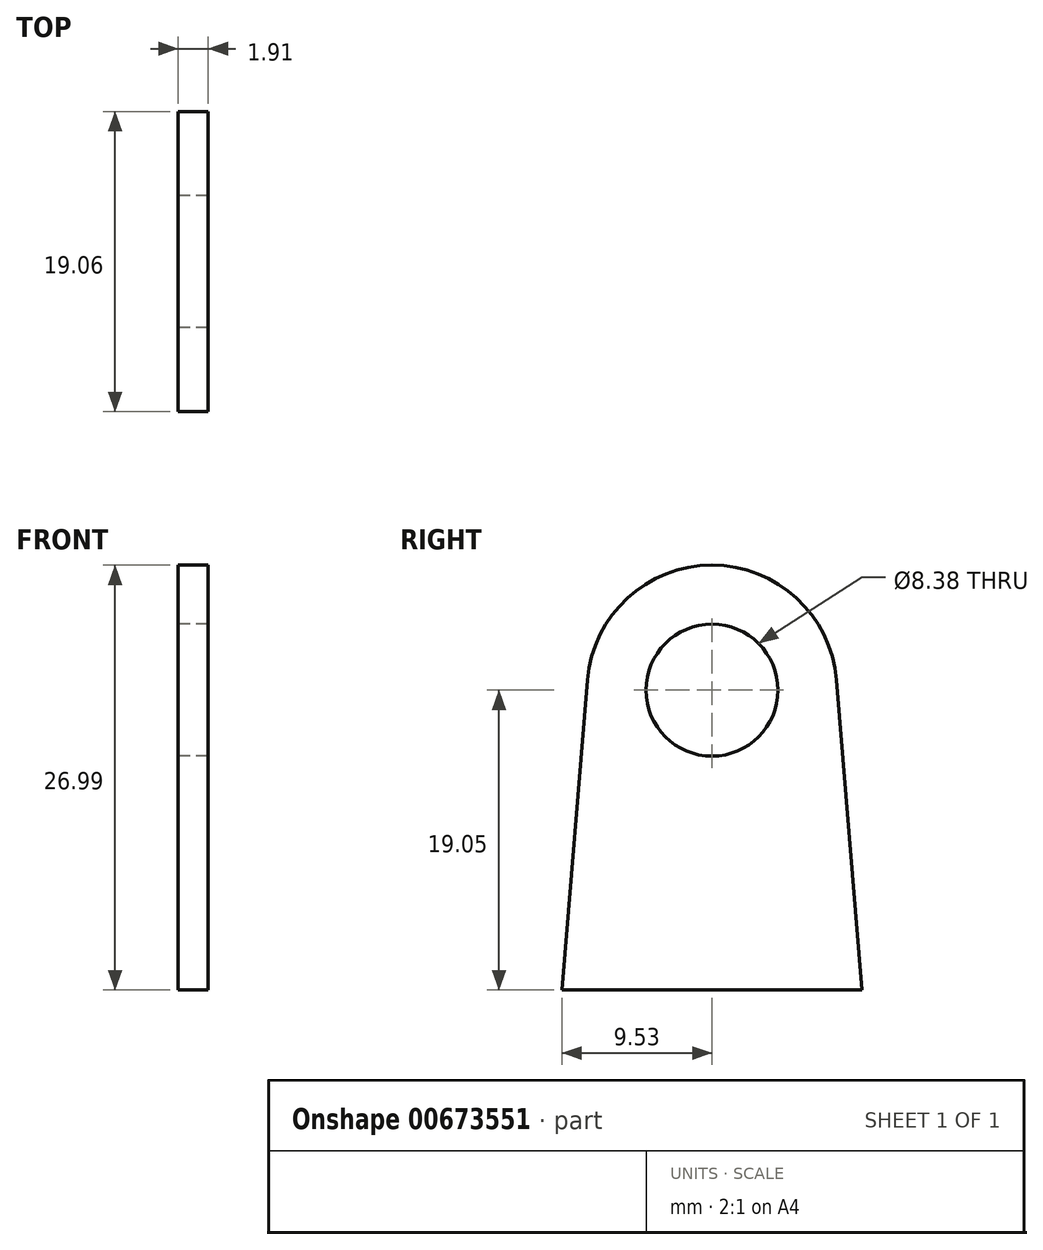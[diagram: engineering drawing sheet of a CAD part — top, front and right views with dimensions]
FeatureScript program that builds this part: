
annotation { "Feature Type Name" : "Feature", "Feature Type Description" : "" }
export const myFeature = defineFeature(function(context is Context, id is Id, definition is map)
    precondition{}
    {
        {
            var Q0;
            Q0=qCreatedBy(makeId("Right.planeOp"),FACE);
            var sketch = newSketch(context, id + "F0", { "sketchPlane" : qUnion([Q0])});
            skCircle(sketch, "E0", {"center": v(0, 19.05) * mm, "radius": 4.2 * mm});
            skArc(sketch, "E1", {"start": v(7.91, 19.7) * mm, "mid": v(0, 26.99) * mm, "end": v(-7.91, 19.7) * mm});
            skLineSegment(sketch, "E2", {"start": v(-9.53, 0) * mm, "end": v(-7.91, 19.7) * mm});
            skLineSegment(sketch, "E3", {"start": v(-9.53, 0) * mm, "end": v(9.53, 0) * mm});
            skLineSegment(sketch, "E4", {"start": v(9.53, 0) * mm, "end": v(7.91, 19.7) * mm});
            skSolve(sketch);
        }
        {
            var Q0;
            Q0=qSketchRegion(id+"F0",true);
            extrude(context, id + "F1", {"entities" : qUnion([Q0]), "depth" : 1.9 * mm, "offsetDistance" : 25.4 * mm});
        }
    });
